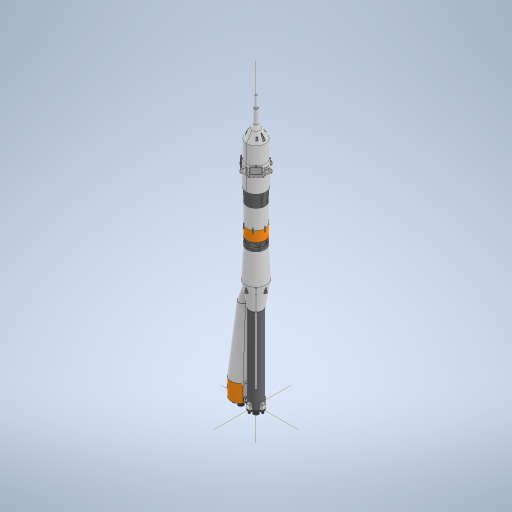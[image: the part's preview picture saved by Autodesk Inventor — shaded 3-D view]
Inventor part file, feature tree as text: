
AUTODESK INVENTOR PART (.ipt)
format: ipt  version: 2023 (Build 270158030, 158C)  size: 14,793,728 bytes
history: native  units: mm
features: fillet x71, sketch x70, extrude x63, other x23, plane x15, revolve x12, pattern_circular x11, sweep x6, mirror x3, chamfer x1, split x1
ambient origin geometry x8: Origin, YZ Plane, XZ Plane, XY Plane, X Axis, Y Axis, Z Axis, Center Point
bodies: Solid17 (feature_tree), Solid18 (feature_tree), Solid19 (feature_tree), Solid20 (feature_tree)
feature tree (276):
  other  "Soyuz Core Stage"
  extrude  "Core Airframe"  Depth=133.0mm TaperAngle=0.0deg
  extrude  "Vernier Housing"  Depth=3.4mm
  extrude  "Main Engine Extrude"  TaperAngle=0.0deg  [1 undecoded]
  extrude  "Main Engine Cut"  Depth=3.4mm
  extrude  "Vernier Nozzels"  Depth=3.4mm
  extrude  "Extrusion11"  Depth=3.4mm
  extrude  "Extrusion12"  Depth=5.5mm
  sweep  "Sweep1"
  sweep  "Booster Nosecone"
  extrude  "Extrusion16"  Depth=4.5mm
  plane  "Work Plane6"
  extrude  "Extrusion17"  Depth=4.5mm
  plane  "Work Plane5"
  extrude  "Extrusion18"  Depth=4.5mm
  fillet  "Fillet11"  Radius=4.5mm
  fillet  "Fillet12"  Radius=6.0mm
  fillet  "Fillet13"  Radius=2.0mm
  fillet  "Fillet14"  Radius=10.5mm
  extrude  "Booster Lock Extrusion"  Depth=2.0mm
  extrude  "Booster Lock Cut"  Depth=10.5mm
  other  "Work Point1"
  plane  "Work Plane1"
  sweep  "Sweep4"
  extrude  "Extrusion26"  TaperAngle=0.0deg  [1 undecoded]
  fillet  "Fillet16"  [1 undecoded]
  plane  "Work Plane4"
  other  "Work Point2"
  plane  "Work Plane2"
  extrude  "Extrusion27"  Depth=5.0mm
  extrude  "Extrusion28"  Depth=5.0mm
  extrude  "Extrusion29"  Depth=5.0mm
  fillet  "Fillet17"  [1 undecoded]
  fillet  "Fillet18"  [1 undecoded]
  fillet  "Fillet19"  [1 undecoded]
  extrude  "Extrusion30"  Depth=9.0mm
  fillet  "Fillet20"  Radius=28.0mm
  fillet  "Fillet21"  Radius=25.0mm
  fillet  "Fillet22"  [1 undecoded]
  extrude  "Extrusion31"  Depth=13.0mm
  extrude  "Extrusion32"  TaperAngle=0.0deg  [1 undecoded]
  extrude  "Extrusion33"  TaperAngle=0.0deg  [1 undecoded]
  extrude  "Extrusion34"  TaperAngle=0.0deg  [1 undecoded]
  fillet  "Fillet23"  [1 undecoded]
  fillet  "Fillet24"  Radius=17.0mm
  fillet  "Fillet25"  Radius=23.0mm
  fillet  "Fillet26"  [1 undecoded]
  extrude  "Extrusion35"  TaperAngle=0.0deg  [1 undecoded]
  extrude  "Extrusion36"  Depth=15.0mm
  extrude  "Extrusion50"  Depth=1.5mm
  fillet  "Fillet75"  [1 undecoded]
  extrude  "Extrusion51"  Depth=3.0mm TaperAngle=0.0deg
  extrude  "Extrusion52"  Depth=0.5mm TaperAngle=0.0deg
  other  "Work Point13"
  sketch  "Sketch86"  dims[d311=15.0mm d312=15.0mm]
  sweep  "Sweep6"
  revolve  "Revolution2"  [1 undecoded]
  pattern_circular  "Circular Pattern5"  [2 undecoded]
  mirror  "Mirror4"
  revolve  "Revolution3"  [1 undecoded]
  fillet  "Fillet76"  Radius=2.0mm
  fillet  "Fillet77"  Radius=21.5mm
  fillet  "Fillet78"  Radius=21.5mm
  fillet  "Fillet79"  Radius=6.2mm
  fillet  "Fillet80"  Radius=6.2mm
  fillet  "Fillet81"  Radius=0.5mm
  fillet  "Fillet82"  Radius=0.5mm
  fillet  "Fillet83"  Radius=0.5mm
  fillet  "Fillet84"  [1 undecoded]
  fillet  "Fillet85"  Radius=0.5mm
  fillet  "Fillet86"  Radius=1.3mm
  extrude  "Extrusion54"  TaperAngle=0.0deg  [1 undecoded]
  fillet  "Fillet91"  Radius=1.3mm
  fillet  "Fillet92"  Radius=3.0mm
  fillet  "Fillet93"  Radius=3.0mm
  pattern_circular  "Circular Pattern6"  [2 undecoded]
  plane  "Work Plane20"
  extrude  "Extrusion56"  TaperAngle=0.0deg  [1 undecoded]
  pattern_circular  "Circular Pattern8"  [2 undecoded]
  extrude  "Extrusion57"  Depth=1.0mm
  extrude  "Extrusion58"  Depth=0.5mm
  fillet  "Fillet94"  [1 undecoded]
  extrude  "Extrusion59"  TaperAngle=0.0deg  [1 undecoded]
  fillet  "Fillet95"  Radius=5.0mm
  pattern_circular  "Circular Pattern9"  [2 undecoded]
  extrude  "Extrusion60"  Depth=0.5mm
  fillet  "Fillet96"  [1 undecoded]
  extrude  "Extrusion61"  Depth=10.0mm TaperAngle=0.0deg
  fillet  "Fillet97"  Radius=0.5mm
  extrude  "Extrusion62"  Depth=0.5mm
  pattern_circular  "Circular Pattern11"  [2 undecoded]
  fillet  "Fillet98"  Radius=1.0mm
  extrude  "Extrusion63"  Depth=0.5mm
  fillet  "Fillet99"  Radius=0.5mm
  fillet  "Fillet100"  [1 undecoded]
  extrude  "Extrusion64"  TaperAngle=0.0deg  [1 undecoded]
  extrude  "Extrusion65"  TaperAngle=0.0deg  [1 undecoded]
  extrude  "Extrusion66"  TaperAngle=0.0deg  [1 undecoded]
  extrude  "Extrusion67"  Depth=0.5mm TaperAngle=0.0deg
  fillet  "Fillet101"  Radius=3.0mm
  plane  "Work Plane24"
  extrude  "Extrusion68"  Depth=0.5mm
  fillet  "Fillet102"  Radius=0.1mm
  extrude  "Extrusion69"  Depth=0.5mm
  pattern_circular  "Circular Pattern12"  [2 undecoded]
  extrude  "Extrusion70"  TaperAngle=0.0deg  [1 undecoded]
  fillet  "Fillet103"  [1 undecoded]
  pattern_circular  "Circular Pattern13"  [2 undecoded]
  extrude  "Extrusion71"  TaperAngle=0.0deg  [1 undecoded]
  extrude  "Extrusion72"  TaperAngle=0.0deg  [1 undecoded]
  extrude  "Extrusion73"  TaperAngle=0.0deg  [1 undecoded]
  fillet  "Fillet105"  [1 undecoded]
  extrude  "Extrusion74"  TaperAngle=0.0deg  [1 undecoded]
  extrude  "Extrusion75"  TaperAngle=0.0deg  [1 undecoded]
  fillet  "Fillet106"  [1 undecoded]
  fillet  "Fillet107"  [1 undecoded]
  other  "Work Point16"
  revolve  "Revolution6"  [1 undecoded]
  other  "Work Point17"
  plane  "Work Plane26"
  extrude  "Extrusion81"  Depth=0.5mm
  fillet  "Fillet114"  Radius=12.5mm
  fillet  "Fillet115"  Radius=12.5mm
  fillet  "Fillet116"  Radius=12.5mm
  fillet  "Fillet117"  [1 undecoded]
  mirror  "Mirror6"
  sweep  "Sweep8"
  pattern_circular  "Circular Pattern14"  [2 undecoded]
  extrude  "Extrusion80"  TaperAngle=0.0deg  [1 undecoded]
  revolve  "Revolution5"  [1 undecoded]
  extrude  "Extrusion82"  TaperAngle=0.0deg  [1 undecoded]
  fillet  "Fillet118"  [1 undecoded]
  other  "Work Point18"
  plane  "Work Plane27"
  extrude  "Extrusion83"  TaperAngle=0.0deg  [1 undecoded]
  sweep  "Sweep9"
  revolve  "Revolution7"  [1 undecoded]
  revolve  "Revolution8"  [1 undecoded]
  revolve  "Revolution9"  [1 undecoded]
  revolve  "Revolution10"  [1 undecoded]
  fillet  "Fillet119"  Radius=6.0mm
  fillet  "Fillet120"  Radius=6.0mm
  fillet  "Fillet121"  Radius=6.0mm
  fillet  "Fillet122"  [1 undecoded]
  fillet  "Fillet123"  [1 undecoded]
  fillet  "Fillet124"  Radius=5.0mm
  plane  "Work Plane30"
  extrude  "Extrusion85"  Depth=1.0mm
  extrude  "Extrusion86"  Depth=1.0mm
  extrude  "Extrusion87"  Depth=0.5mm
  extrude  "Extrusion88"  Depth=0.5mm
  fillet  "Fillet125"  Radius=1.0mm
  fillet  "Fillet126"  [1 undecoded]
  fillet  "Fillet127"  Radius=2.0mm
  fillet  "Fillet128"  [1 undecoded]
  extrude  "Extrusion89"  Depth=0.5mm
  extrude  "Extrusion90"  Depth=1.0mm
  fillet  "Fillet129"  [1 undecoded]
  fillet  "Fillet130"  Radius=1.0mm
  fillet  "Fillet131"  Radius=0.781667mm
  extrude  "Extrusion92"  Depth=0.5mm
  extrude  "Extrusion93"  Depth=0.5mm
  fillet  "Fillet134"  Radius=12.5mm
  fillet  "Fillet135"  Radius=0.5mm
  fillet  "Fillet136"  [1 undecoded]
  fillet  "Fillet138"  Radius=0.5mm
  pattern_circular  "Circular Pattern15"  [2 undecoded]
  other  "Work Point19"
  plane  "Work Plane31"
  extrude  "Extrusion94"  Depth=0.5mm
  fillet  "Fillet139"  [1 undecoded]
  revolve  "Revolution11"  [1 undecoded]
  chamfer  "Chamfer3"  Distance=1.377412mm
  fillet  "Fillet140"  Radius=1.377mm
  fillet  "Fillet141"  Radius=4.5mm
  fillet  "Fillet142"  Radius=1.0mm
  plane  "Work Plane32"
  revolve  "Revolution12"  [1 undecoded]
  fillet  "Fillet143"  Radius=4.5mm
  pattern_circular  "Circular Pattern16"  [2 undecoded]
  fillet  "Fillet144"  Radius=1.0mm
  pattern_circular  "Circular Pattern17"  [2 undecoded]
  mirror  "Mirror7"
  split  "Split1"
  sketch  "Sketch5"  dims[d0=20.0mm d1=133.0mm d2=0.0mm]
  sketch  "Sketch6"  dims[d7=0.0mm d9=3.4mm]
  sketch  "Sketch15"  dims[d10=3.4mm d12=0.0mm]
  sketch  "Sketch16"  dims[d15=3.4mm d18=3.4mm]
  other  "Soyuz Booster"
  sketch  "Sketch28"  dims[d20=3.4mm d21=3.4mm]
  sketch  "Sketch29"  dims[d25=3.4mm d26=3.4mm]
  sketch  "Sketch31"  dims[d33=7.0mm d34=0.0mm d47=5.5mm]
  sketch  "Sketch34"  dims[d48=5.5mm d49=5.5mm]
  sketch  "Sketch35"  dims[d50=5.5mm d52=4.5mm]
  sketch  "Sketch42"  dims[d57=4.5mm d58=4.5mm d59=4.5mm d60=6.0mm d61=2.094395mm d62=2.0mm d63=10.5mm]
  sketch  "Sketch43"  dims[d64=2.0mm d65=2.0mm]
  sketch  "Sketch45"  dims[d66=2.0mm d67=10.5mm]
  sketch  "Sketch51"  dims[d68=10.5mm d69=10.5mm]
  sketch  "Sketch52"  dims[d70=0.0mm d71=0.0mm d72=0.0mm]
  sketch  "Sketch53"  dims[d73=0.0mm d74=5.0mm d75=1.396263mm]
  sketch  "Sketch54"  dims[d76=5.0mm d77=5.0mm]
  sketch  "Sketch55"  dims[d78=5.0mm d79=5.0mm d80=0.0mm d81=0.0mm d82=0.0mm]
  sketch  "Sketch56"  dims[d83=0.0mm d85=9.0mm d86=-1.396263mm d156=28.0mm d160=25.0mm d161=0.0mm]
  other  "Core Stage Part 2"
  sketch  "Sketch57"  dims[d166=13.0mm d167=13.0mm d168=13.0mm d171=13.0mm]
  sketch  "Sketch81"  dims[d174=27.0mm d175=0.0mm d177=0.0mm]
  sketch  "Sketch82"  dims[d178=0.0mm d179=0.0mm]
  sketch  "Sketch83"  dims[d180=38.0mm d181=1.658063mm d236=0.0mm d237=0.0mm d278=17.0mm d280=23.0mm d281=-0.610865mm d282=0.0mm]
  other  "Interstage 1"
  sketch  "Sketch85"  dims[d304=0.0mm d309=0.0mm]
  other  "Srf3"
  sketch  "3D Sketch5"
  other  "Project to Surface5"
  sketch  "Sketch87"  dims[d313=19.0mm d314=1.5mm d316=-2.356194mm d317=0.0mm]
  other  "Project to Surface7"
  sketch  "Sketch88"  dims[d318=0.0mm d330=3.0mm d331=0.0mm]
  sketch  "Sketch89"  dims[d334=0.5mm d335=0.0mm d338=0.5mm d339=0.0mm]
  sketch  "Sketch91"  dims[d342=3.0mm d343=3.0mm]
  plane  "Work Plane19"
  sketch  "Sketch93"  dims[d344=3.0mm d345=6.0mm]
  sketch  "Sketch94"  dims[d346=1.2mm]
  other  "Interstage 2"
  sketch  "Sketch95"  dims[d347=1.2mm]
  other  "2nd Stage"
  sketch  "Sketch96"  dims[d348=1.2mm]
  sketch  "Sketch97"  dims[d349=1.2mm]
  sketch  "Sketch100"  dims[d350=0.0mm]
  other  "Srf4"
  sketch  "Sketch103"  dims[d351=0.0mm]
  sketch  "Sketch104"  dims[d352=0.0mm]
  sketch  "Sketch105"  dims[d353=0.0mm]
  sketch  "Sketch107"  dims[d354=14.5mm]
  sketch  "Sketch108"  dims[d355=14.5mm]
  sketch  "Sketch109"  dims[d356=14.5mm]
  sketch  "Sketch111"  dims[d357=14.5mm]
  sketch  "Sketch112"  dims[d358=11.5mm d359=1.745329mm]
  sketch  "Sketch113"  dims[d361=2.2mm]
  sketch  "Sketch114"  dims[d362=1.6mm]
  sketch  "Sketch115"  dims[d363=0.0mm]
  sketch  "Sketch116"  dims[d364=4.1mm d365=-1.745329mm]
  other  "2nd Stage Part 2"
  sketch  "Sketch117"  dims[d366=0.0mm]
  sketch  "Sketch118"  dims[d367=1.6mm]
  sketch  "Sketch120"  dims[d368=2.2mm]
  sketch  "Sketch121"  dims[d369=0.0mm]
  sketch  "Sketch128"  dims[d370=1.6mm]
  other  "Fairing"
  sketch  "Sketch130"  dims[d371=2.2mm]
  sketch  "Sketch132"  dims[d372=1.6mm]
  sketch  "Sketch134"  dims[d373=0.0mm]
  sketch  "Sketch135"  dims[d374=2.2mm]
  sketch  "Sketch139"  dims[d397=5.5mm d398=4.5mm d400=5.5mm d401=4.5mm d402=4.5mm d403=5.5mm d404=4.5mm d406=5.5mm d410=2.094395mm d411=6.0mm]
  sketch  "Sketch140"  dims[d412=5.0mm d413=0.0mm d414=5.0mm d415=0.0mm d416=0.0mm d417=5.0mm d418=0.0mm d419=5.0mm d421=-1.396263mm d422=9.0mm]
  other  "Escape Tower"
  plane  "Work Plane28"
  plane  "Work Plane29"
  other  "Grid Fins"
  sketch  "Sketch145"  dims[d423=0.0mm]
  sketch  "Sketch146"  dims[d424=0.0mm]
  sketch  "Sketch149"  dims[d425=0.0mm]
  sketch  "Sketch150"  dims[d426=0.0mm]
  sketch  "Sketch152"  dims[d427=9.0mm]
  sketch  "Sketch153"  dims[d428=9.0mm]
  sketch  "Sketch154"  dims[d429=9.0mm]
  sketch  "Sketch156"  dims[d430=9.0mm]
  sketch  "Sketch157"  dims[d431=6.0mm]
  other  "Pattern of Fairing:1"
  other  "Pattern of Grid Fins:2"
  sketch  "Sketch159"  dims[d432=0.0mm d446=1.396263mm d447=5.0mm d449=2.0mm d450=2.0mm d452=21.5mm d453=21.5mm d454=6.2mm d455=6.2mm d456=0.5mm d459=0.5mm d460=0.5mm d461=0.0mm d464=0.5mm d465=1.3mm d466=0.0mm d467=1.3mm d468=3.0mm d470=3.0mm d472=0.0mm d473=0.0mm d475=6.0mm d476=1.0mm d477=6.0mm d478=0.0mm d479=-0.202458mm d480=0.0mm d481=5.0mm d482=2.0mm d483=2.0mm d484=0.0mm d485=10.0mm d486=0.0mm d487=0.5mm d489=3.0mm d490=1.0mm d491=1.0mm d492=28.0mm d493=0.5mm d494=0.0mm d518=0.0mm d521=0.0mm d522=0.0mm d524=0.0mm d525=0.5mm d526=0.0mm d527=3.0mm d528=3.0mm d529=0.1mm d530=20.0mm d531=7.0mm d532=0.0mm d538=0.0mm d539=0.0mm d540=0.0mm d541=0.0mm d542=0.0mm d543=0.0mm d544=0.0mm d545=0.0mm d546=0.0mm d547=0.0mm d548=0.0mm d549=0.0mm d550=12.5mm d551=12.5mm d553=12.5mm d554=12.5mm d556=0.0mm d557=0.0mm d561=0.0mm d562=0.0mm d563=0.0mm d564=0.0mm d566=0.0mm d567=0.0mm d568=0.0mm d571=0.0mm d572=0.0mm d573=0.0mm d575=6.0mm d576=6.0mm d577=6.0mm d578=6.0mm d579=0.0mm d581=0.0mm d582=5.0mm d583=-6.108652mm d584=1.0mm d585=1.0mm d593=2.0mm d594=3.0mm d604=1.0mm d608=0.0mm d609=2.0mm d610=0.0mm d611=3.0mm d612=1.0mm d614=0.0mm d617=1.0mm d618=0.781667mm d619=2.5mm d649=12.5mm d650=12.5mm d651=0.5mm d652=0.0mm d653=0.5mm d654=4.5mm d655=4.5mm d657=0.0mm d658=1.0mm d659=1.377412mm d660=1.377mm d661=4.5mm d662=1.0mm d663=0.5mm d664=0.0mm d665=4.5mm d666=1.377mm d667=1.0mm d668=4.5mm d669=1.377mm d670=1.0mm d671=0.5mm d672=0.0mm d673=4.5mm d674=1.377mm d675=4.5mm d676=1.377mm d677=1.0mm d678=1.0mm d679=0.5mm d680=0.0mm d681=4.5mm d682=4.5mm d683=1.377mm d684=1.377mm d685=1.0mm d686=1.0mm d687=0.5mm d688=0.0mm d689=0.5mm d690=0.2mm d691=0.3mm d692=1.0mm d694=0.0mm d695=0.0mm d696=0.1mm d697=5.0mm d698=0.0mm d699=0.0mm d700=0.0mm d702=50.0mm d703=-0.541052mm d709=0.0mm d993=0.0mm d994=0.0mm d995=2.5mm d996=5.0mm d997=0.0mm d998=8.0mm d999=0.0mm d1000=0.0mm d1001=0.0mm d1002=0.0mm d1003=0.0mm d1004=0.0mm d1005=4.0mm d1006=0.0mm d1007=0.0mm d1008=0.0mm d1009=0.0mm d1010=0.0mm d1011=0.0mm d1012=0.0mm d1013=4.1mm d1014=0.0mm d1026=45.0deg d1030=0.0mm d1031=0.0mm d1034=10.0mm d1035=3.0mm d1036=0.0mm d1037=0.0mm d1038=0.1mm d1039=0.0mm d1040=2.5mm d1041=2.5mm d1042=0.9mm d1048=2.5mm d1049=2.6mm d1050=90.0deg d1051=60.0mm d1052=360.0deg d1054=1.5mm d1057=0.4mm d1058=90.0deg d1059=0.2mm d1060=0.7mm d1061=0.4mm d1062=1.0mm d1063=0.5mm d1064=0.2mm d1065=0.2mm d1066=0.2mm d1067=0.2mm d1068=0.2mm d1069=0.2mm d1070=0.1mm d1083=0.5mm d1084=0.3mm d1085=2.0mm d1086=0.0mm d1087=1.3mm d1088=0.0mm d1089=0.7mm d1090=0.5mm d1091=0.7mm d1092=60.0mm d1093=360.0deg d1103=-1.0mm d1104=0.0mm d1105=0.0mm d1106=0.0mm d1107=0.0mm d1108=30.0mm d1109=1.25mm d1110=1.4mm d1111=0.0mm d1112=1.25mm d1116=40.0mm d1117=360.0deg d1119=0.0mm d1120=0.0mm d1121=0.0mm d1122=0.0mm d1123=0.0mm d1124=0.0mm d1125=16.0mm d1126=0.0mm d1127=0.0mm d1128=0.0mm d1129=0.0mm d1130=30.0mm d1131=0.0mm d1132=0.1mm d1133=1.7mm d1134=14.0mm d1135=5.0mm d1136=0.0mm d1137=0.8mm d1138=60.0mm d1139=360.0deg d1141=0.0mm d1142=3.0mm d1143=0.0mm d1144=0.5mm d1145=1.0mm d1146=6.0mm d1147=0.0mm d1148=8.0mm d1149=0.0mm d1150=3.0mm d1151=9.0mm d1152=6.981317mm d1153=9.6mm d1154=90.0deg d1193=3.5mm d1194=1.2mm d1195=0.0mm d1196=2.5mm d1197=1.8mm d1200=2.0mm d1201=10.0mm d1203=0.3mm d1204=0.2mm d1205=9.397169mm d1206=1.165699mm d1207=1.2mm d1208=2.0mm d1209=2.0mm d1210=0.0mm d1211=60.0mm d1212=360.0deg d1214=8.0mm d1215=0.0mm d1216=0.0mm d1217=20.0mm d1218=2.0mm d1219=0.0mm d1220=0.2mm d1221=0.2mm d1222=5.5mm d1223=4.5mm d1224=4.5mm d1228=5.0mm d1229=4.0mm d1230=2.094395mm d1231=-2.094395mm d1232=0.0mm d1233=0.0mm d1234=0.0mm d1235=5.0mm d1236=4.014257mm d1238=0.0mm d1239=0.0mm d1240=1.5mm d1241=10.5mm d1242=-1.396263mm d1243=2.0mm d1244=8.5mm d1245=0.0mm d1246=4.0mm d1247=1.745329mm d1248=0.8mm d1249=1.5mm d1250=3.0mm d1251=8.5mm d1252=2.8mm d1253=0.0mm d1254=1.4mm d1258=6.8mm d1259=0.872665mm d1260=0.0mm d1261=0.0mm d1262=0.0mm d1263=0.0mm d1264=0.55mm d1265=0.0mm d1266=40.0mm d1267=360.0deg d1270=0.0mm d1271=0.0mm d1272=0.0mm d1273=3.55mm d1274=0.0mm d1275=0.8mm d1276=60.0mm d1277=360.0deg d1282=20.0mm d1283=0.349066mm d1286=4.0mm d1287=0.0mm d1288=0.2mm d1289=1.0mm d1290=0.0mm d1291=0.2mm d1292=3.5mm d1293=5.0mm d1294=7.0mm d1295=0.0mm d1296=5.0mm d1297=5.0mm d1298=0.0mm d1299=1.0mm d1300=1.0mm d1310=0.0mm d1311=0.0mm d1313=11.5mm d1316=0.3mm d1317=0.3mm d1318=3.066164mm d1319=2.367748mm d1320=9.41mm d1321=4.705mm d1324=1.81mm d1330=0.0mm d1331=0.0mm d1333=3.0mm d1361=20.0mm d1362=360.0deg d1372=0.0mm d1375=0.0mm d1391=1.0mm d1392=1.3mm d1393=2.0mm d1394=2.0mm d1395=2.0mm d1396=2.0mm d1397=1.0mm d1398=1.0mm d1399=1.0mm d1400=1.0mm d1401=1.0mm d1402=1.0mm d1403=13.566164mm d1404=12.266164mm d1405=13.566164mm d1406=12.266164mm d1407=13.566164mm d1408=12.266164mm d1409=13.566164mm d1410=12.266164mm d1411=2.0mm d1412=90.0deg d1413=1.2mm d1414=2.5mm d1417=3.0mm d1418=0.0mm d1424=3.0mm d1425=15.53343mm d1429=180.0deg d1430=23.0mm d1431=12.2mm d1432=45.0deg d1433=2.5mm d1434=2.5mm d1435=3.4mm d1436=3.4mm d1437=0.0mm d1438=0.0mm d1439=1.3mm d1440=0.0mm d1441=0.5mm d1442=0.4mm d1443=0.4mm d1444=0.4mm d1445=11.586164mm d1446=0.0mm d1447=0.0mm d1448=0.0mm d1449=0.0mm d1452=0.0mm d1453=1.3mm d1454=0.0mm d1455=0.0mm d1456=0.0mm d1458=13.566164mm d1459=12.266164mm d1460=12.266164mm d1461=13.566164mm d1462=2.0mm d1463=1.5mm d1464=0.0mm d1465=0.1mm d1469=5.0mm d1470=5.0mm d1471=20.0mm d1473=1.071mm d1474=0.0mm d1475=0.0mm d1476=0.0mm d1477=0.0mm d1478=0.0mm d1479=0.0mm d1482=19.3mm d1483=0.0mm d1484=16.057029mm d1485=3.0mm d1486=0.0mm d1487=0.0mm d1490=0.0mm d1497=15.184364mm d1498=15.0mm d1499=180.0deg d1500=27.0mm d1501=15.620697mm d1502=180.0deg d1504=60.0deg d1513=13.856406mm d1514=180.0deg d1528=14.0mm d1529=3.579724mm d1531=1.0mm d1532=1.000457mm d1533=0.917096mm d1534=1.0mm d1540=2.0mm d1541=1.329428mm d1543=1.5mm d1545=4.997278mm d1546=0.0mm d1547=3.0mm d1552=2.7mm d1554=30.892328mm d1555=2.0mm d1556=3.250296mm d1557=6.497278mm d1560=0.0mm d1561=21.46755mm d1562=25.0mm d1563=1.5mm d1564=0.0mm d1566=20.071286mm d1567=37.0mm d1568=1.0mm d1569=1.0mm d1570=27.0mm d1571=45.0mm d1572=90.0deg d1574=0.917096mm d1575=0.4mm d1576=0.4mm d1577=0.4mm d1578=0.1mm d1579=0.1mm d1580=0.2mm d1583=2.0mm d1593=1.0mm d1594=1.0mm d1596=0.5mm d1597=2.5mm d1598=3.5mm d1599=3.5mm d1600=3.5mm d1601=2.0mm d1602=0.0mm d1603=0.7mm d1604=0.7mm d1605=4.0mm d1606=0.7mm d1607=0.7mm d1608=0.0mm d1609=0.0mm d1610=0.0mm d1611=0.0mm d1612=0.0mm d1613=0.3mm d1614=0.0mm d1615=0.2mm d1616=2.0mm d1617=1.0mm d1618=2.0mm d1619=1.0mm d1621=100.0mm d1622=2.0mm d1623=2.0mm d1624=2.0mm d1625=0.0mm d1626=0.0mm d1627=0.9mm d1628=0.1mm d1629=0.1mm d1630=0.1mm d1632=1.0mm d1633=0.75mm d1634=0.75mm d1635=0.0mm d1636=0.0mm d1640=7.0mm d1641=7.0mm d1642=3.5mm d1643=0.7mm d1644=6.0mm d1645=0.0mm d1646=2.0mm d1649=0.0mm d1650=2.0mm d1651=2.25mm d1652=4.5mm d1653=0.0mm d1654=0.0mm d1655=4.0mm d1656=1.0mm d1657=0.5mm d1667=1.0mm d1668=0.0mm d1669=0.0mm d1670=0.0mm d1674=0.8mm d1676=0.8mm d1677=0.5mm d1678=0.5mm d1679=1.5mm d1680=1.7mm d1681=0.0mm d1682=2.0mm d1683=0.2mm d1684=0.1mm d1686=0.1mm d1687=20.0mm d1688=90.0deg d1690=3.5mm d1691=0.0mm d1692=4.5mm d1693=4.5mm d1694=0.0mm d1695=2.0mm d1696=0.0mm d1697=1.0mm d1698=4.0mm d1699=2.0mm d1700=45.0deg d1701=12.0mm d1702=3.0mm d1703=10.7mm d1705=5.0mm d1706=12.0mm d1707=2.443461mm d1708=1.0mm d1709=2.0mm d1710=45.0deg d1711=0.5mm d1712=0.5mm d1713=0.5mm d1714=4.5mm d1715=5.5mm d1716=8.0mm d1717=8.5mm d1718=9.424778mm d1719=3.3mm d1720=2.3mm d1721=1.745329mm d1722=0.5mm d1723=20.0mm d1724=19.198622mm d1726=0.5mm d1731=0.5mm d1732=0.5mm d1733=0.5mm d1734=0.5mm d1735=0.5mm d1736=0.5mm d1737=0.5mm d1738=0.5mm d1739=0.5mm d1740=0.5mm d1741=0.5mm d1742=0.5mm d1743=0.5mm d1744=0.5mm d1745=0.5mm d1746=0.5mm d1747=0.5mm d1748=0.5mm d1749=0.5mm d1755=0.5mm d1756=0.5mm d1757=0.5mm d1758=0.5mm d1759=0.5mm d1760=0.5mm d1763=0.5mm d1764=0.5mm d1766=0.5mm d1767=0.5mm d1768=0.5mm d1769=0.5mm d1770=0.5mm d1771=0.5mm d1772=0.5mm d1773=0.5mm d1774=0.5mm d1775=0.5mm d1776=0.5mm d1777=0.5mm d1778=0.5mm d1779=0.5mm d1780=0.5mm d1781=0.5mm d1782=0.5mm d1783=0.5mm d1784=0.5mm d1785=0.5mm d1786=0.5mm d1787=0.5mm d1788=0.5mm d1789=0.5mm d1790=0.5mm d1791=0.5mm d1792=0.5mm d1793=0.5mm d1794=20.0mm d1795=90.0deg d194=0.5mm d195=0.872665mm d196=0.5mm d197=0.872665mm d261=0.5mm d262=0.872665mm d263=0.5mm d264=0.872665mm d808=0.5mm d809=0.872665mm d810=0.5mm d811=0.872665mm d1255=0.872665mm d1351=0.5mm d1352=0.872665mm d1353=0.5mm d1354=0.872665mm]
  extrude  "Extrusion23"  Depth=0.5mm
  extrude  "Extrusion24"  Depth=1.0mm
  extrude  "Extrusion25"  Depth=0.5mm TaperAngle=0.0deg
  revolve  "RevolutionSrf2"  [1 undecoded]
  revolve  "RevolutionSrf3"  [1 undecoded]
  sketch  "Sketch39"  dims[d53=4.5mm d54=4.5mm]
  sketch  "Sketch40"  dims[d55=4.5mm d56=4.5mm]
note: 80 required parameter values undecoded (feature->parameter linkage not recoverable at this tier; creation-order binding heuristic only, values carry confidence <= 0.55)